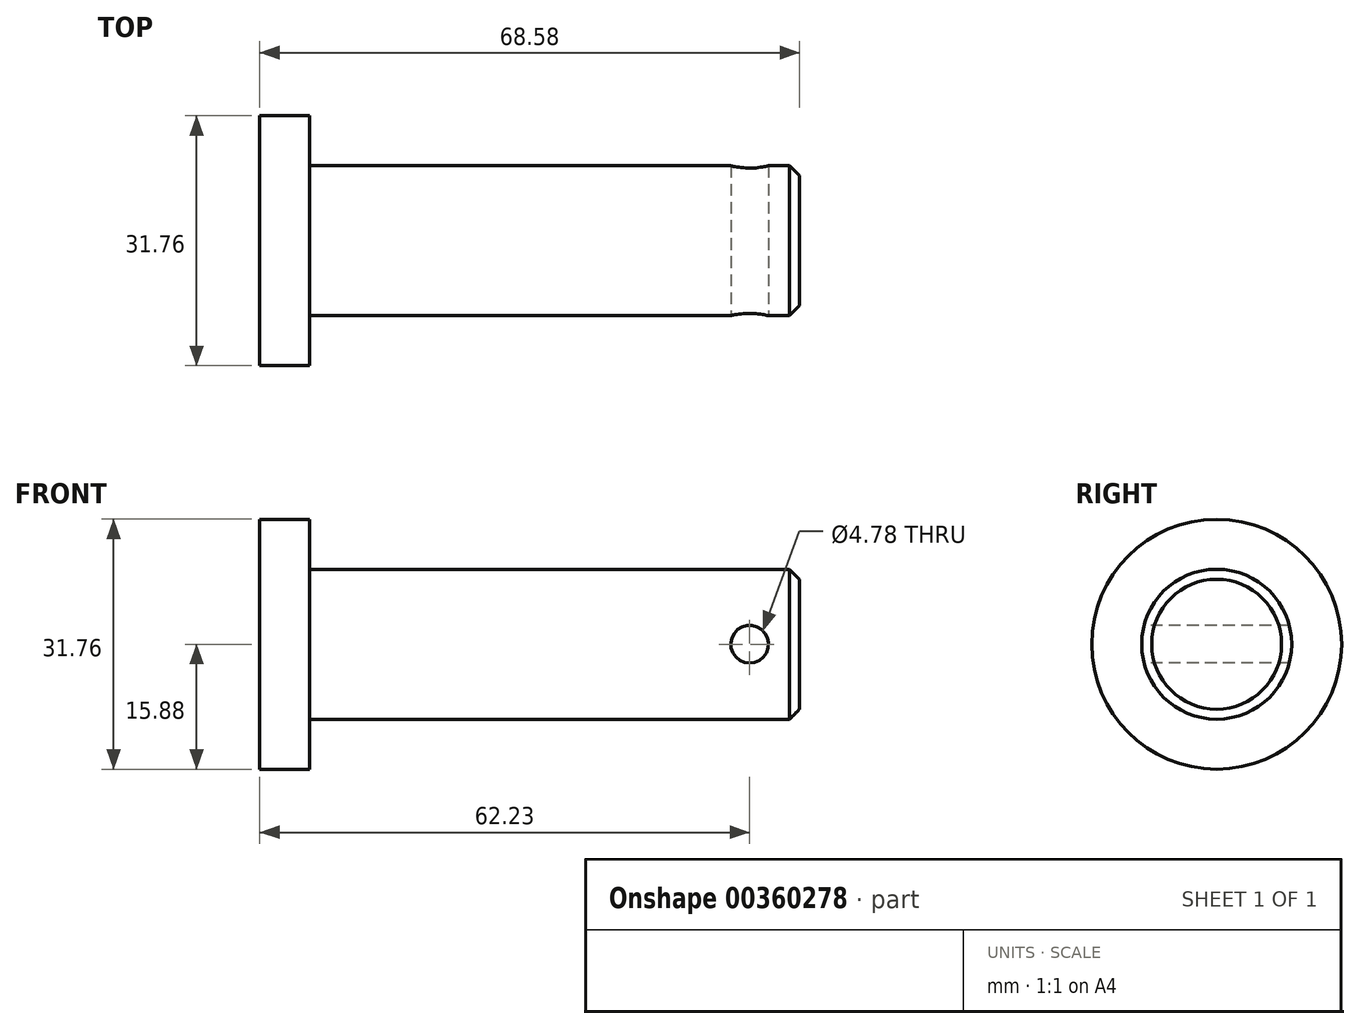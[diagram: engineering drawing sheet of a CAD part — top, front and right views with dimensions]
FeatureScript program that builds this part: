
annotation { "Feature Type Name" : "Feature", "Feature Type Description" : "" }
export const myFeature = defineFeature(function(context is Context, id is Id, definition is map)
    precondition{}
    {
        {
            var Q0;
            Q0=qCreatedBy(makeId("Right.planeOp"),FACE);
            var sketch = newSketch(context, id + "F0", { "sketchPlane" : qUnion([Q0])});
            skCircle(sketch, "E0", {"center": v(0, 0) * mm, "radius": 15.88 * mm});
            skSolve(sketch);
        }
        {
            var Q0;
            Q0 = qSketchRegion(id + "F0", true);
            extrude(context, id + "F1", {"entities" : qUnion([Q0]), "oppositeDirection" : true, "depth" : 6.35 * mm});
        }
        {
            var Q0;
            Q0=makeQuery(id+"F1.opExtrude","CAP_FACE",FACE,{"disambiguationData":[OSD([sQuery(id+"F0.wireOp",EDGE,"E0")])],"isStart":true});
            var sketch = newSketch(context, id + "F2", { "sketchPlane" : qUnion([Q0])});
            skCircle(sketch, "E1", {"center": v(0, 0) * mm, "radius": 9.53 * mm});
            skSolve(sketch);
        }
        {
            var Q0;
            Q0 = qSketchRegion(id + "F2", true);
            extrude(context, id + "F3", {"entities" : qUnion([Q0]), "operationType" : NewBodyOperationType.ADD, "depth" : 62.23 * mm});
        }
        {
            var Q0;
            Q0=qCreatedBy(makeId("Front.planeOp"),FACE);
            var sketch = newSketch(context, id + "F4", { "sketchPlane" : qUnion([Q0])});
            skLineSegment(sketch, "E2", {"start": v(-20.67, 0) * mm, "end": v(93.22, 0) * mm, "construction": true});
            skCircle(sketch, "E3", {"center": v(55.88, 0) * mm, "radius": 2.39 * mm});
            skSolve(sketch);
        }
        {
            var Q0;
            Q0 = qSketchRegion(id + "F4", true);
            extrude(context, id + "F5", {"entities" : qUnion([Q0]), "operationType" : NewBodyOperationType.REMOVE, "endBound" : BoundingType.THROUGH_ALL, "oppositeDirection" : true, "depth" : 25.4 * mm, "hasSecondDirection" : true, "secondDirectionBound" : SecondDirectionBoundingType.THROUGH_ALL, "secondDirectionOppositeDirection" : false, "secondDirectionDepth" : 25.4 * mm});
        }
        {
            var Q0;
            Q0=makeQuery(id+"F3.opExtrude","CAP_EDGE",EDGE,{"disambiguationData":[OSD([sQuery(id+"F2.wireOp",EDGE,"E1")])],"isStart":false});
            chamfer(context, id + "F6", {"entities" : qUnion([Q0]), "chamferType" : ChamferType.OFFSET_ANGLE, "width" : 1.27 * mm, "oppositeDirection" : false, "angle" : 45 * degree, "tangentPropagation" : true});
        }
    });
